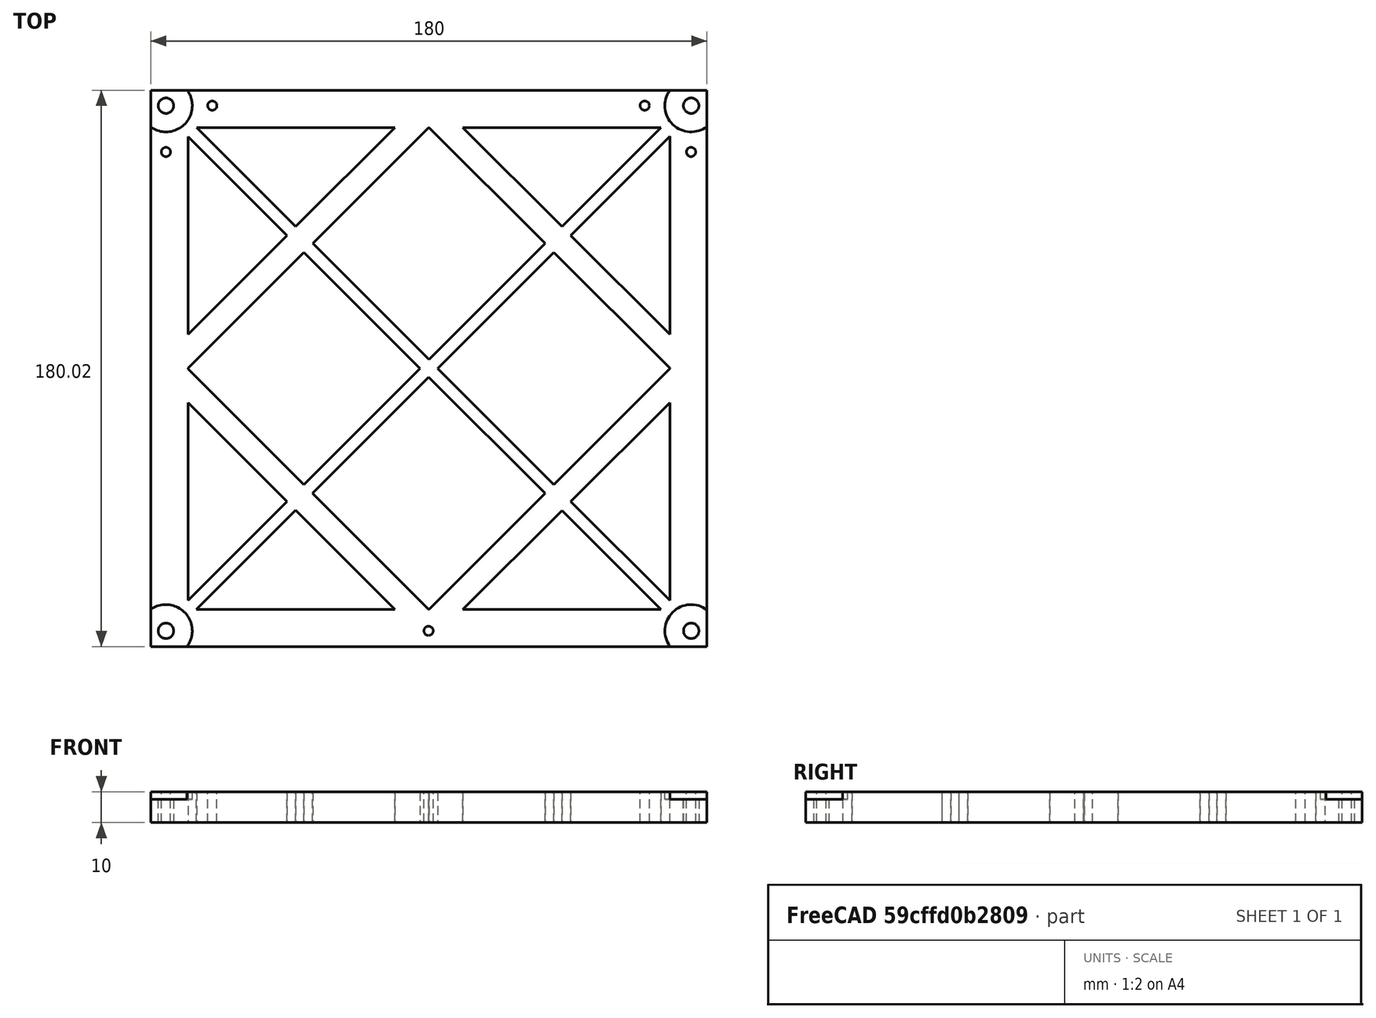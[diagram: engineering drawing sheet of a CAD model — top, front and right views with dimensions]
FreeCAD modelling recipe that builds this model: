
FCSTD DOCUMENT  (FreeCAD 2024.2R37179 (Git))
Label: Bed_mount_Center
License: All rights reserved
LicenseURL: http://en.wikipedia.org/wiki/All_rights_reserved
objects: Part::Feature×1, PartDesign::FeatureBase×1, PartDesign::Pad×1, Sketcher::SketchObject×1, PartDesign::Pocket×1, PartDesign::Body×1
note: 8 computed .brp shape members not serialized (recipe doc carries the construction recipe); baked Part::Feature solids carry a one-line shape summary decoded from their .brp

FEATURE [Part::Feature] Pocket007
  shape: bbox 180 x 180 x 10 mm, 102 faces (baked)
FEATURE [PartDesign::FeatureBase] BaseFeature
  BaseFeature = -> Pocket007
  Suppressed = false
FEATURE [PartDesign::Pad] Pad
  BaseFeature = -> BaseFeature
  Direction = (0,0,-1)
  Length = 10
  Length2 = 10
  Profile = -> BaseFeature [Face99,Face100,Face102,Face101,Face98]
  Refine = true
  Suppressed = false
  Type = 3
  UpToFace = -> BaseFeature [Face2]
FEATURE [Sketcher::SketchObject] Sketch
  AttachmentSupport = -> [Pad]
  FullyConstrained = false
  MapMode = 5
  Placement = pos=(0,0,10) rot=(0,0,1;0rad)
  sketch-geometry (4):
    g0: Circle CenterX=591.599 CenterY=-50.6769 CenterZ=0 NormalX=0 NormalY=0 NormalZ=1 AngleXU=0 Radius=2.5
    g1: Circle CenterX=421.589 CenterY=-50.6928 CenterZ=0 NormalX=0 NormalY=0 NormalZ=1 AngleXU=0 Radius=2.5
    g2: Circle CenterX=591.567 CenterY=119.32 CenterZ=0 NormalX=0 NormalY=0 NormalZ=1 AngleXU=0 Radius=2.5
    g3: Circle CenterX=421.599 CenterY=119.315 CenterZ=0 NormalX=0 NormalY=0 NormalZ=1 AngleXU=0 Radius=2.5
  constraints (4):
    c: Diameter(g1) = 5
    c: Diameter(g0) = 5
    c: Diameter(g2) = 5
    c: Diameter(g3) = 5
FEATURE [PartDesign::Pocket] Pocket
  BaseFeature = -> Pad
  Direction = (0,0,-1)
  Length = 35
  Length2 = 5
  Profile = -> Sketch
  ReferenceAxis = -> Sketch [N_Axis]
  Refine = true
  Suppressed = false
  Type = 0
FEATURE [PartDesign::Body] Body
  BaseFeature = -> Pocket007
  Group = -> [BaseFeature,Pad,Sketch,Pocket]
  Origin = -> Origin
  Tip = -> Pocket
